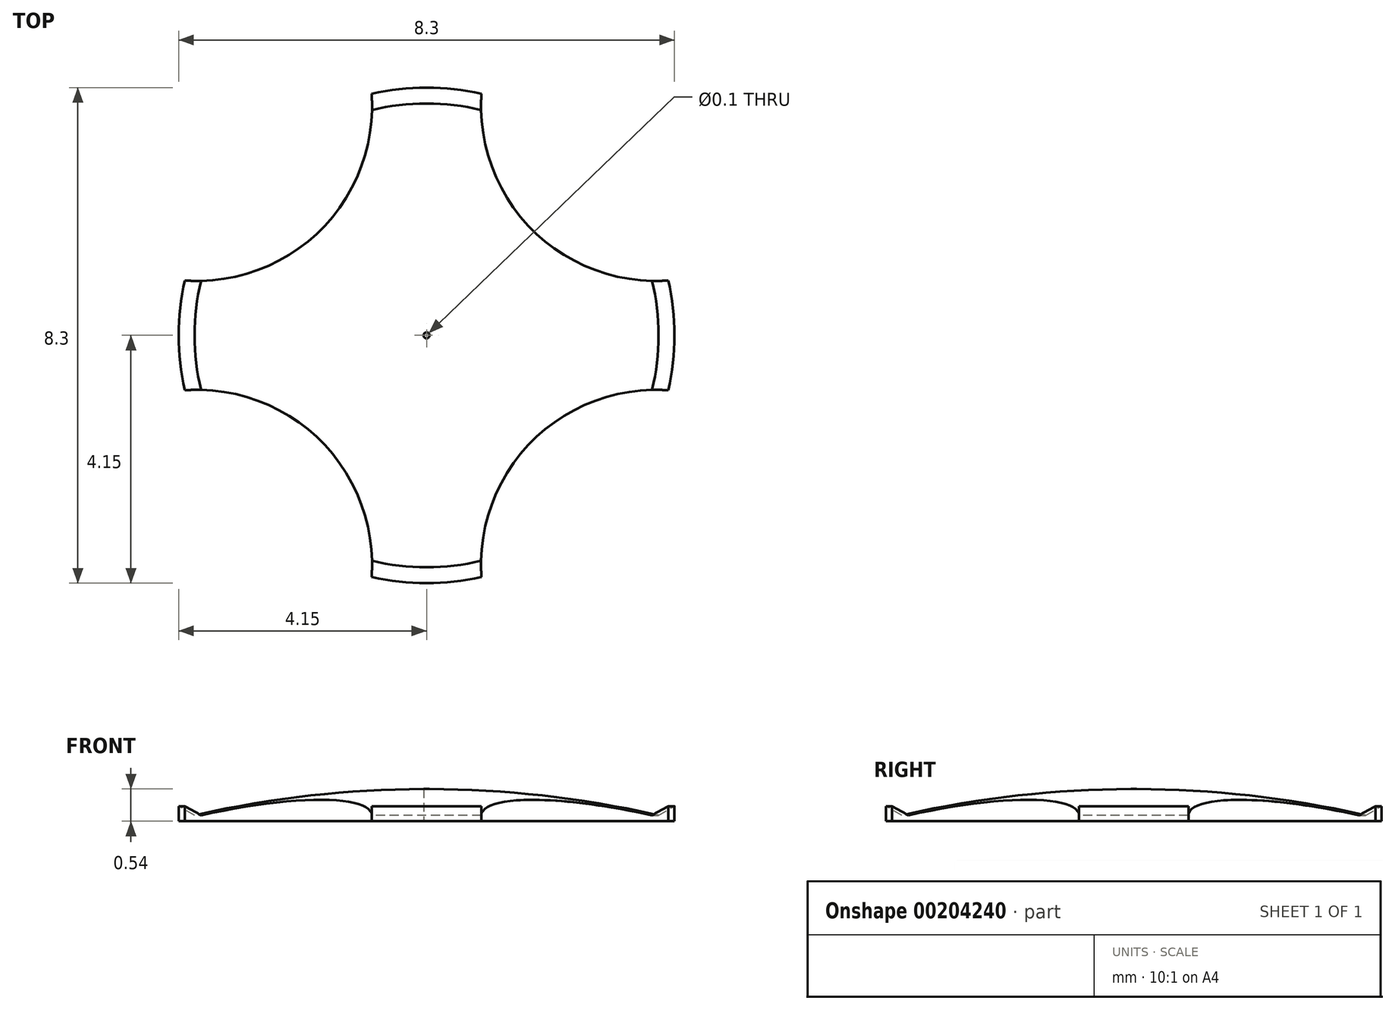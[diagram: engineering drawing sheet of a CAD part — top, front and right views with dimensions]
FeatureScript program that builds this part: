
annotation { "Feature Type Name" : "Feature", "Feature Type Description" : "" }
export const myFeature = defineFeature(function(context is Context, id is Id, definition is map)
    precondition{}
    {
        {
            var Q0;
            Q0=qCreatedBy(makeId("Front.planeOp"),FACE);
            var sketch = newSketch(context, id + "F0", { "sketchPlane" : qUnion([Q0])});
            skArc(sketch, "E0", {"start": v(3.89, 0.1) * mm, "mid": v(1.95, 0.43) * mm, "end": v(0, 0.54) * mm});
            skLineSegment(sketch, "E1", {"start": v(0, 0) * mm, "end": v(0, 0.54) * mm});
            skLineSegment(sketch, "E2", {"start": v(3.88, 0.1) * mm, "end": v(4.15, 0.25) * mm});
            skLineSegment(sketch, "E3", {"start": v(4.15, 0.25) * mm, "end": v(4.15, 0) * mm});
            skLineSegment(sketch, "E4", {"start": v(4.15, 0) * mm, "end": v(0, 0) * mm});
            skSolve(sketch);
        }
        {
            var Q0;
            Q0=qSketchRegion(id+"F0",true);
            var Q1;
            Q1=sQuery(id+"F0.wireOp",EDGE,"E1");
            revolve(context, id + "F1", {"entities" : qUnion([Q0]), "axis" : qUnion([Q1]), "revolveType" : RevolveType.FULL});
        }
        {
            var Q0;
            Q0=makeQuery(id+"F1.opRevolve","SWEPT_FACE",FACE,{"disambiguationData":[OSD([sQuery(id+"F0.wireOp",EDGE,"E4")])]});
            var sketch = newSketch(context, id + "F2", { "sketchPlane" : qUnion([Q0])});
            skCircle(sketch, "E5", {"center": v(0, 0) * mm, "radius": 2.5 * mm, "construction": true});
            skLineSegment(sketch, "E6", {"start": v(0, 0) * mm, "end": v(-3.83, 3.83) * mm, "construction": true});
            skLineSegment(sketch, "E7", {"start": v(0, 0) * mm, "end": v(0, 16.1) * mm, "construction": true});
            skCircle(sketch, "E8", {"center": v(-3.83, 3.83) * mm, "radius": 2.92 * mm});
            skLineSegment(sketch, "E9", {"start": v(0, 0) * mm, "end": v(3.83, 3.83) * mm, "construction": true});
            skCircle(sketch, "E10", {"center": v(3.83, 3.83) * mm, "radius": 2.92 * mm});
            skLineSegment(sketch, "E11", {"start": v(-3.83, 3.83) * mm, "end": v(-0.92, 4.05) * mm, "construction": true});
            skLineSegment(sketch, "E12", {"start": v(3.83, 3.83) * mm, "end": v(0.92, 4.05) * mm, "construction": true});
            skLineSegment(sketch, "E13", {"start": v(0, 0) * mm, "end": v(-3.83, -3.83) * mm, "construction": true});
            skLineSegment(sketch, "E14", {"start": v(0, 0) * mm, "end": v(3.83, -3.83) * mm, "construction": true});
            skCircle(sketch, "E15", {"center": v(-3.83, -3.83) * mm, "radius": 2.92 * mm});
            skCircle(sketch, "E16", {"center": v(3.83, -3.83) * mm, "radius": 2.92 * mm});
            skSolve(sketch);
        }
        {
            var Q0;
            Q0=qSketchRegion(id+"F2",true);
            extrude(context, id + "F3", {"entities" : qUnion([Q0]), "operationType" : NewBodyOperationType.REMOVE, "endBound" : BoundingType.THROUGH_ALL, "oppositeDirection" : true, "depth" : 25 * mm});
        }
        {
            var Q0;
            Q0=makeQuery(id+"F1.opRevolve","SWEPT_FACE",FACE,{"disambiguationData":[OSD([sQuery(id+"F0.wireOp",EDGE,"E4")])]});
            var sketch = newSketch(context, id + "F4", { "sketchPlane" : qUnion([Q0])});
            skCircle(sketch, "E17", {"center": v(0, 0) * mm, "radius": 0.05 * mm});
            skSolve(sketch);
        }
        {
            var Q0;
            Q0 = qSketchRegion(id + "F4", true);
            extrude(context, id + "F5", {"entities" : qUnion([Q0]), "operationType" : NewBodyOperationType.REMOVE, "oppositeDirection" : true, "depth" : 25 * mm});
        }
    });
